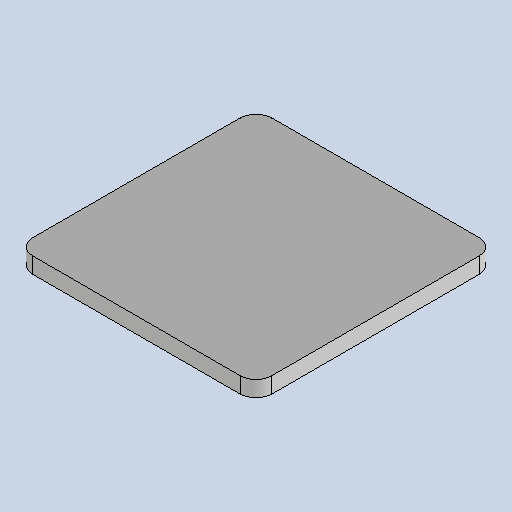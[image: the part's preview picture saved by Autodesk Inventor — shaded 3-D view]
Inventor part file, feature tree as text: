
AUTODESK INVENTOR PART (.ipt)
format: ipt  version: 2025.1 (Build 291241020, 241B)  size: 140,288 bytes
history: native  units: mm
features: other x2, sheet_metal_op x1, chamfer x1, sketch x1
ambient origin geometry x8: Origin, YZ Plane, XZ Plane, XY Plane, X Axis, Y Axis, Z Axis, Center Point
bodies: Body1 (feature_tree)
feature tree (5):
  sheet_metal_op  "Face3"
  chamfer  "Corner Round1"
  sketch  "Sketch1"  dims[d154=30.0mm d155=30.0mm d156=2.0mm d178=2.0mm]
  other  "Plate5"
  other  "Definition1"
